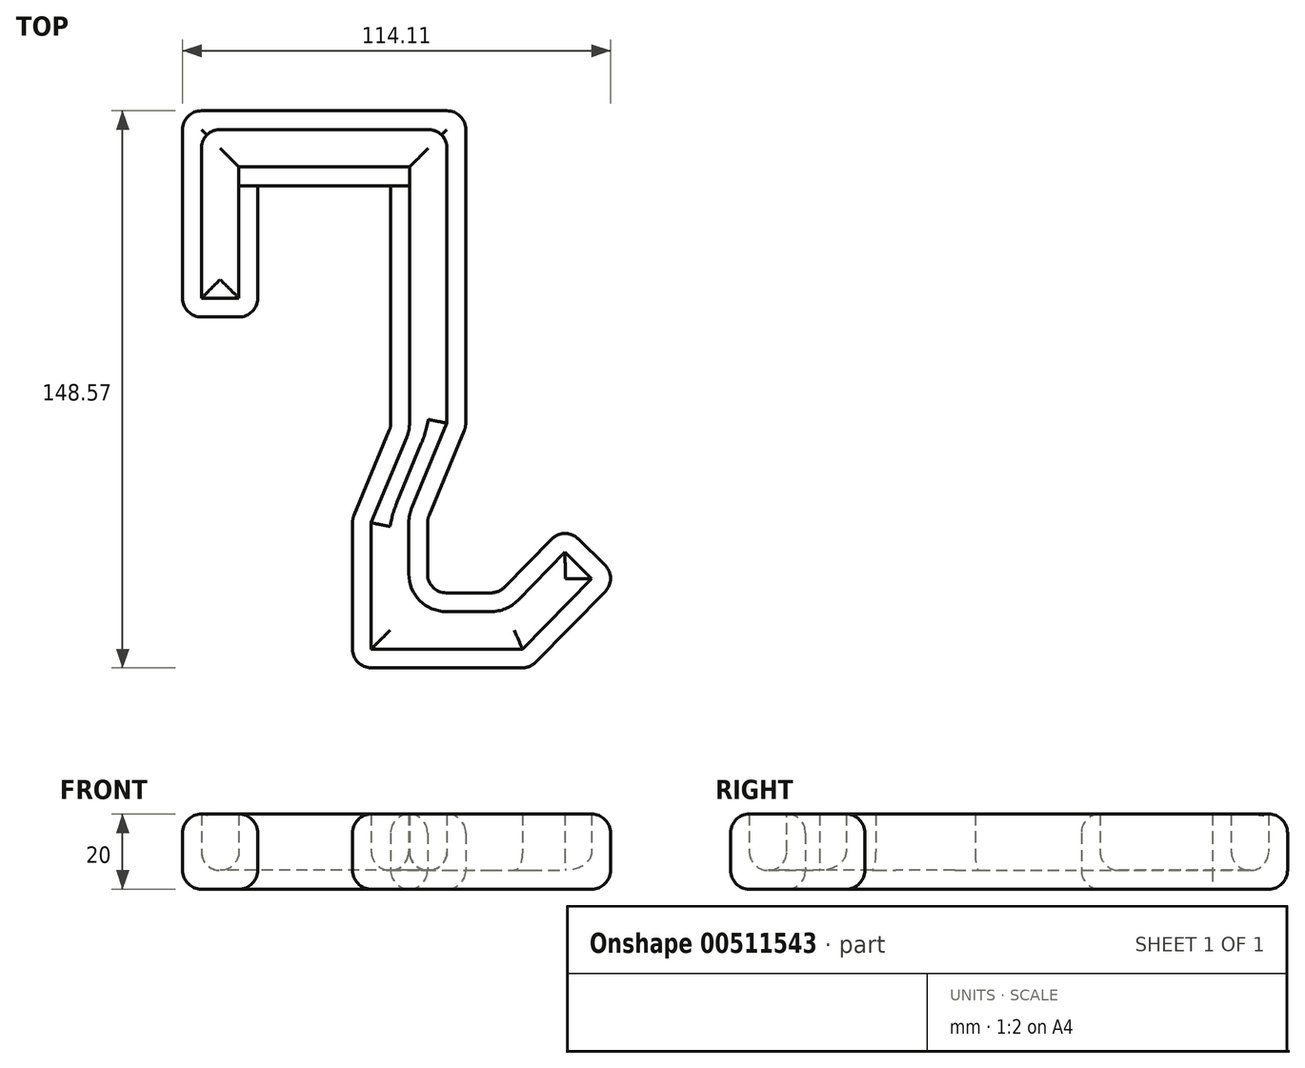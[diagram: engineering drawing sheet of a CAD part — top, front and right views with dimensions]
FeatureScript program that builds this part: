
annotation { "Feature Type Name" : "Feature", "Feature Type Description" : "" }
export const myFeature = defineFeature(function(context is Context, id is Id, definition is map)
    precondition{}
    {
        {
            var Q0;
            Q0=qCreatedBy(makeId("Top.planeOp"),FACE);
            var sketch = newSketch(context, id + "F0", { "sketchPlane" : qUnion([Q0])});
            skLineSegment(sketch, "E0", {"start": v(-75.5, 10.12) * mm, "end": v(-75.5, 55.12) * mm});
            skLineSegment(sketch, "E1", {"start": v(-70.5, 60.12) * mm, "end": v(-5, 60.12) * mm});
            skLineSegment(sketch, "E2", {"start": v(0, 55.12) * mm, "end": v(0, -23.19) * mm});
            skLineSegment(sketch, "E3", {"start": v(-0.38, -25.1) * mm, "end": v(-9.8, -47.84) * mm});
            skLineSegment(sketch, "E4", {"start": v(-10.19, -49.75) * mm, "end": v(-10.19, -63.45) * mm});
            skLineSegment(sketch, "E5", {"start": v(-5.19, -68.45) * mm, "end": v(6.7, -68.45) * mm});
            skLineSegment(sketch, "E6", {"start": v(10.27, -66.95) * mm, "end": v(22.91, -54.1) * mm});
            skLineSegment(sketch, "E7", {"start": v(29.98, -54.04) * mm, "end": v(37.11, -61.05) * mm});
            skLineSegment(sketch, "E8", {"start": v(37.17, -68.12) * mm, "end": v(18.65, -86.95) * mm});
            skLineSegment(sketch, "E9", {"start": v(15.09, -88.45) * mm, "end": v(-25.19, -88.45) * mm});
            skLineSegment(sketch, "E10", {"start": v(-30.19, -83.45) * mm, "end": v(-30.19, -49.75) * mm});
            skLineSegment(sketch, "E11", {"start": v(-29.8, -47.84) * mm, "end": v(-20.38, -25.1) * mm});
            skLineSegment(sketch, "E12", {"start": v(-20, -23.19) * mm, "end": v(-20, 40.12) * mm});
            skLineSegment(sketch, "E13", {"start": v(-20, 40.12) * mm, "end": v(-55.5, 40.12) * mm});
            skLineSegment(sketch, "E14", {"start": v(-55.5, 40.12) * mm, "end": v(-55.5, 10.12) * mm});
            skLineSegment(sketch, "E15", {"start": v(-60.5, 5.12) * mm, "end": v(-70.5, 5.12) * mm});
            skPoint(sketch, "E16.visualSharp", {"position": v(-75.5, 60.12) * mm});
            skArc(sketch, "E16.filletArc", {"start": v(-70.5, 60.12) * mm, "mid": v(-74.04, 58.65) * mm, "end": v(-75.5, 55.12) * mm});
            skPoint(sketch, "E17.visualSharp", {"position": v(-75.5, 5.12) * mm});
            skArc(sketch, "E17.filletArc", {"start": v(-75.5, 10.12) * mm, "mid": v(-74.04, 6.58) * mm, "end": v(-70.5, 5.12) * mm});
            skPoint(sketch, "E18.visualSharp", {"position": v(-55.5, 5.12) * mm});
            skArc(sketch, "E18.filletArc", {"start": v(-60.5, 5.12) * mm, "mid": v(-56.96, 6.58) * mm, "end": v(-55.5, 10.12) * mm});
            skPoint(sketch, "E19.visualSharp", {"position": v(0, 60.12) * mm});
            skArc(sketch, "E19.filletArc", {"start": v(0, 55.12) * mm, "mid": v(-1.46, 58.65) * mm, "end": v(-5, 60.12) * mm});
            skPoint(sketch, "E20.visualSharp", {"position": v(0, -24.18) * mm});
            skArc(sketch, "E20.filletArc", {"start": v(-0.38, -25.1) * mm, "mid": v(-0.1, -24.17) * mm, "end": v(0, -23.19) * mm});
            skPoint(sketch, "E21.visualSharp", {"position": v(-10.19, -48.76) * mm});
            skArc(sketch, "E21.filletArc", {"start": v(-9.8, -47.84) * mm, "mid": v(-10.1, -48.78) * mm, "end": v(-10.19, -49.75) * mm});
            skPoint(sketch, "E22.visualSharp", {"position": v(-30.19, -48.76) * mm});
            skArc(sketch, "E22.filletArc", {"start": v(-29.8, -47.84) * mm, "mid": v(-30.1, -48.78) * mm, "end": v(-30.19, -49.75) * mm});
            skPoint(sketch, "E23.visualSharp", {"position": v(-20, -24.18) * mm});
            skArc(sketch, "E23.filletArc", {"start": v(-20.38, -25.1) * mm, "mid": v(-20.1, -24.17) * mm, "end": v(-20, -23.19) * mm});
            skPoint(sketch, "E24.visualSharp", {"position": v(-10.19, -68.45) * mm});
            skArc(sketch, "E24.filletArc", {"start": v(-10.19, -63.45) * mm, "mid": v(-8.72, -66.98) * mm, "end": v(-5.19, -68.45) * mm});
            skPoint(sketch, "E25.visualSharp", {"position": v(-30.19, -88.45) * mm});
            skArc(sketch, "E25.filletArc", {"start": v(-30.19, -83.45) * mm, "mid": v(-28.72, -86.98) * mm, "end": v(-25.19, -88.45) * mm});
            skPoint(sketch, "E26.visualSharp", {"position": v(17.18, -88.45) * mm});
            skArc(sketch, "E26.filletArc", {"start": v(15.09, -88.45) * mm, "mid": v(17.02, -88.06) * mm, "end": v(18.65, -86.95) * mm});
            skPoint(sketch, "E27.visualSharp", {"position": v(8.8, -68.45) * mm});
            skArc(sketch, "E27.filletArc", {"start": v(6.7, -68.45) * mm, "mid": v(8.64, -68.06) * mm, "end": v(10.27, -66.95) * mm});
            skPoint(sketch, "E28.visualSharp", {"position": v(26.42, -50.53) * mm});
            skArc(sketch, "E28.filletArc", {"start": v(29.98, -54.04) * mm, "mid": v(26.44, -52.6) * mm, "end": v(22.91, -54.1) * mm});
            skPoint(sketch, "E29.visualSharp", {"position": v(40.68, -64.56) * mm});
            skArc(sketch, "E29.filletArc", {"start": v(37.17, -68.12) * mm, "mid": v(38.6, -64.58) * mm, "end": v(37.11, -61.05) * mm});
            skSolve(sketch);
        }
        {
            var Q0;
            Q0 = qSketchRegion(id + "F0", true);
            extrude(context, id + "F1", {"entities" : qUnion([Q0]), "depth" : 20 * mm});
        }
        {
            var Q0;
            Q0=makeQuery(id+"F1.opExtrude","CAP_EDGE",EDGE,{"disambiguationData":[OSD([sQuery(id+"F0.wireOp",EDGE,"E1")])],"isStart":false});
            var Q1;
            Q1=makeQuery(id+"F1.opExtrude","CAP_EDGE",EDGE,{"disambiguationData":[OSD([sQuery(id+"F0.wireOp",EDGE,"E2")])],"isStart":true});
            fillet(context, id + "F2", {"entities" : qUnion([Q0, Q1]), "radius" : 5 * mm, "tangentPropagation" : true, "allowEdgeOverflow" : false});
        }
        {
            var Q0;
            Q0=makeQuery(id+"F1.opExtrude","CAP_FACE",FACE,{"disambiguationData":[OSD([sQuery(id+"F0.wireOp",EDGE,"E0"),sQuery(id+"F0.wireOp",EDGE,"E1"),sQuery(id+"F0.wireOp",EDGE,"E2"),sQuery(id+"F0.wireOp",EDGE,"E3"),sQuery(id+"F0.wireOp",EDGE,"E4"),sQuery(id+"F0.wireOp",EDGE,"E5"),sQuery(id+"F0.wireOp",EDGE,"E6"),sQuery(id+"F0.wireOp",EDGE,"E7"),sQuery(id+"F0.wireOp",EDGE,"E8"),sQuery(id+"F0.wireOp",EDGE,"E9"),sQuery(id+"F0.wireOp",EDGE,"E10"),sQuery(id+"F0.wireOp",EDGE,"E11"),sQuery(id+"F0.wireOp",EDGE,"E12"),sQuery(id+"F0.wireOp",EDGE,"E13"),sQuery(id+"F0.wireOp",EDGE,"E14"),sQuery(id+"F0.wireOp",EDGE,"E15"),sQuery(id+"F0.wireOp",EDGE,"E16.filletArc"),sQuery(id+"F0.wireOp",EDGE,"E17.filletArc"),sQuery(id+"F0.wireOp",EDGE,"E18.filletArc"),sQuery(id+"F0.wireOp",EDGE,"E19.filletArc"),sQuery(id+"F0.wireOp",EDGE,"E20.filletArc"),sQuery(id+"F0.wireOp",EDGE,"E21.filletArc"),sQuery(id+"F0.wireOp",EDGE,"E22.filletArc"),sQuery(id+"F0.wireOp",EDGE,"E23.filletArc"),sQuery(id+"F0.wireOp",EDGE,"E24.filletArc"),sQuery(id+"F0.wireOp",EDGE,"E25.filletArc"),sQuery(id+"F0.wireOp",EDGE,"E26.filletArc"),sQuery(id+"F0.wireOp",EDGE,"E27.filletArc"),sQuery(id+"F0.wireOp",EDGE,"E28.filletArc"),sQuery(id+"F0.wireOp",EDGE,"E29.filletArc")])],"isStart":false});
            shell(context, id + "F3", {"entities" : qUnion([Q0]), "thickness" : 5 * mm});
        }
        {
            var Q0;
            {var subQ0=sQuery(id+"F0.wireOp",EDGE,"E1");Q0=makeQuery(id+"F3.opShell","OFFSET_EDGE",EDGE,{"disambiguationData":[OSD([subQ0]),TDD([makeQuery(id+"F2.opFillet","BLEND_EDGE",EDGE,{"blendedFrom":[makeQuery(id+"F1.opExtrude","CAP_EDGE",EDGE,{"disambiguationData":[OSD([subQ0])],"isStart":true}),makeQuery(id+"F1.opExtrude","SWEPT_FACE",FACE,{"disambiguationData":[OSD([subQ0])]})],"blendedInto":[makeQuery(id+"F1.opExtrude","SWEPT_FACE",FACE,{"disambiguationData":[OSD([subQ0])]})]})])]});}
            fillet(context, id + "F4", {"entities" : qUnion([Q0]), "radius" : 5 * mm, "tangentPropagation" : true, "allowEdgeOverflow" : false});
        }
        {
            var Q0;
            Q0=makeQuery(id+"F3.opShell","OFFSET_FACE",FACE,{"disambiguationData":[OSD([sQuery(id+"F0.wireOp",EDGE,"E0"),sQuery(id+"F0.wireOp",EDGE,"E1"),sQuery(id+"F0.wireOp",EDGE,"E2"),sQuery(id+"F0.wireOp",EDGE,"E3"),sQuery(id+"F0.wireOp",EDGE,"E4"),sQuery(id+"F0.wireOp",EDGE,"E5"),sQuery(id+"F0.wireOp",EDGE,"E6"),sQuery(id+"F0.wireOp",EDGE,"E7"),sQuery(id+"F0.wireOp",EDGE,"E8"),sQuery(id+"F0.wireOp",EDGE,"E9"),sQuery(id+"F0.wireOp",EDGE,"E10"),sQuery(id+"F0.wireOp",EDGE,"E11"),sQuery(id+"F0.wireOp",EDGE,"E12"),sQuery(id+"F0.wireOp",EDGE,"E13"),sQuery(id+"F0.wireOp",EDGE,"E14"),sQuery(id+"F0.wireOp",EDGE,"E15"),sQuery(id+"F0.wireOp",EDGE,"E16.filletArc"),sQuery(id+"F0.wireOp",EDGE,"E17.filletArc"),sQuery(id+"F0.wireOp",EDGE,"E18.filletArc"),sQuery(id+"F0.wireOp",EDGE,"E19.filletArc"),sQuery(id+"F0.wireOp",EDGE,"E20.filletArc"),sQuery(id+"F0.wireOp",EDGE,"E21.filletArc"),sQuery(id+"F0.wireOp",EDGE,"E22.filletArc"),sQuery(id+"F0.wireOp",EDGE,"E23.filletArc"),sQuery(id+"F0.wireOp",EDGE,"E24.filletArc"),sQuery(id+"F0.wireOp",EDGE,"E25.filletArc"),sQuery(id+"F0.wireOp",EDGE,"E26.filletArc"),sQuery(id+"F0.wireOp",EDGE,"E27.filletArc"),sQuery(id+"F0.wireOp",EDGE,"E28.filletArc"),sQuery(id+"F0.wireOp",EDGE,"E29.filletArc")])]});
            fillet(context, id + "F5", {"entities" : qUnion([Q0]), "radius" : 5 * mm, "tangentPropagation" : true, "allowEdgeOverflow" : false});
        }
    });
